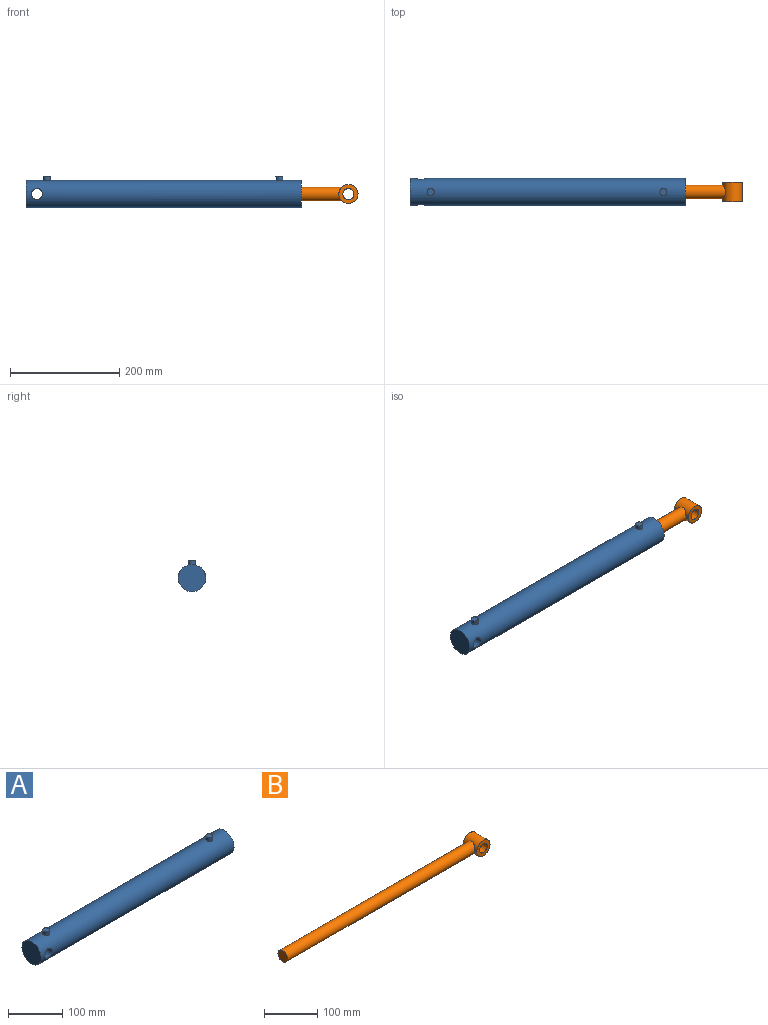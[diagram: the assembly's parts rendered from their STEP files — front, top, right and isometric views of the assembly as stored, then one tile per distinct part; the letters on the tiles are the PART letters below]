
ASSEMBLY  parts=2 mates=1
PART A: 15 faces, bbox 504x50x57.5 mm
  f0: cylinder r=25mm len=504mm, axis (-1,0,0), area 78242.1mm2, adj f1,f2,f3,f4,f6
  f1: plane 50x50mm, normal (1,0,0), area 1963.5mm2, adj f0
  f2: plane 50x50mm, normal (-1,0,0), area 1963.5mm2, adj f0
  f3: cylinder r=10.12mm len=50mm, axis (0,-1,0), area 3046.2mm2, adj f0
  f4: cylinder r=6.5mm len=13mm, axis (0,0,-1), area 323.8mm2, adj f0,f5
  f5: plane 13x13mm, normal (0,0,1), area 132.7mm2, adj f4
  f6: cylinder r=6.5mm len=13mm, axis (0,0,-1), area 323.8mm2, adj f0,f7
  f7: plane 13x13mm, normal (0,0,1), area 132.7mm2, adj f6
  f8: cylinder r=20mm len=424mm, axis (-1,0,0), area 53172.9mm2, adj f9,f10,f11,f14
  f9: plane 40x38.91mm, normal (-1,0,0), area 1228.8mm2, adj f8,f13,f14
  f10: plane 40x39.02mm, normal (1,0,0), area 1229.7mm2, adj f8,f11,f12
  f11: cylinder r=6.5mm len=12.37mm, axis (0,0,-1), area 34.1mm2, adj f8,f10,f12
  f12: plane 12.37x4.5mm, normal (0,0,-1), area 40.8mm2, adj f10,f11
  f13: plane 13x6.5mm, normal (0,0,-1), area 66.4mm2, adj f9,f14
  f14: cylinder r=6.5mm len=13mm, axis (0,0,-1), area 40.1mm2, adj f8,f9,f13
PART B: 6 faces, bbox 533x36x35 mm
  f0: cylinder r=10.12mm len=36mm, axis (0,1,0), area 2290.2mm2, adj f2,f3
  f1: cylinder r=17.5mm len=36mm, axis (0,1,0), area 3427.6mm2, adj f2,f3,f4
  f2: plane 35x35mm, normal (0,-1,0), area 640.1mm2, adj f0,f1
  f3: plane 35x35mm, normal (0,1,0), area 640.1mm2, adj f0,f1
  f4: cylinder r=12.5mm len=503.25mm, axis (1,0,0), area 39309.7mm2, adj f1,f5
  f5: plane 25x25mm, normal (-1,0,0), area 490.9mm2, adj f4
PLACE A t=(-162.71,52.58,-45.31)mm fixed
PLACE B t=(-162.37,52.58,-45.31)mm
MATE slider B.f4 <-> A.f0  axis (1,0,0) through (165.29,52.58,-45.31)mm
